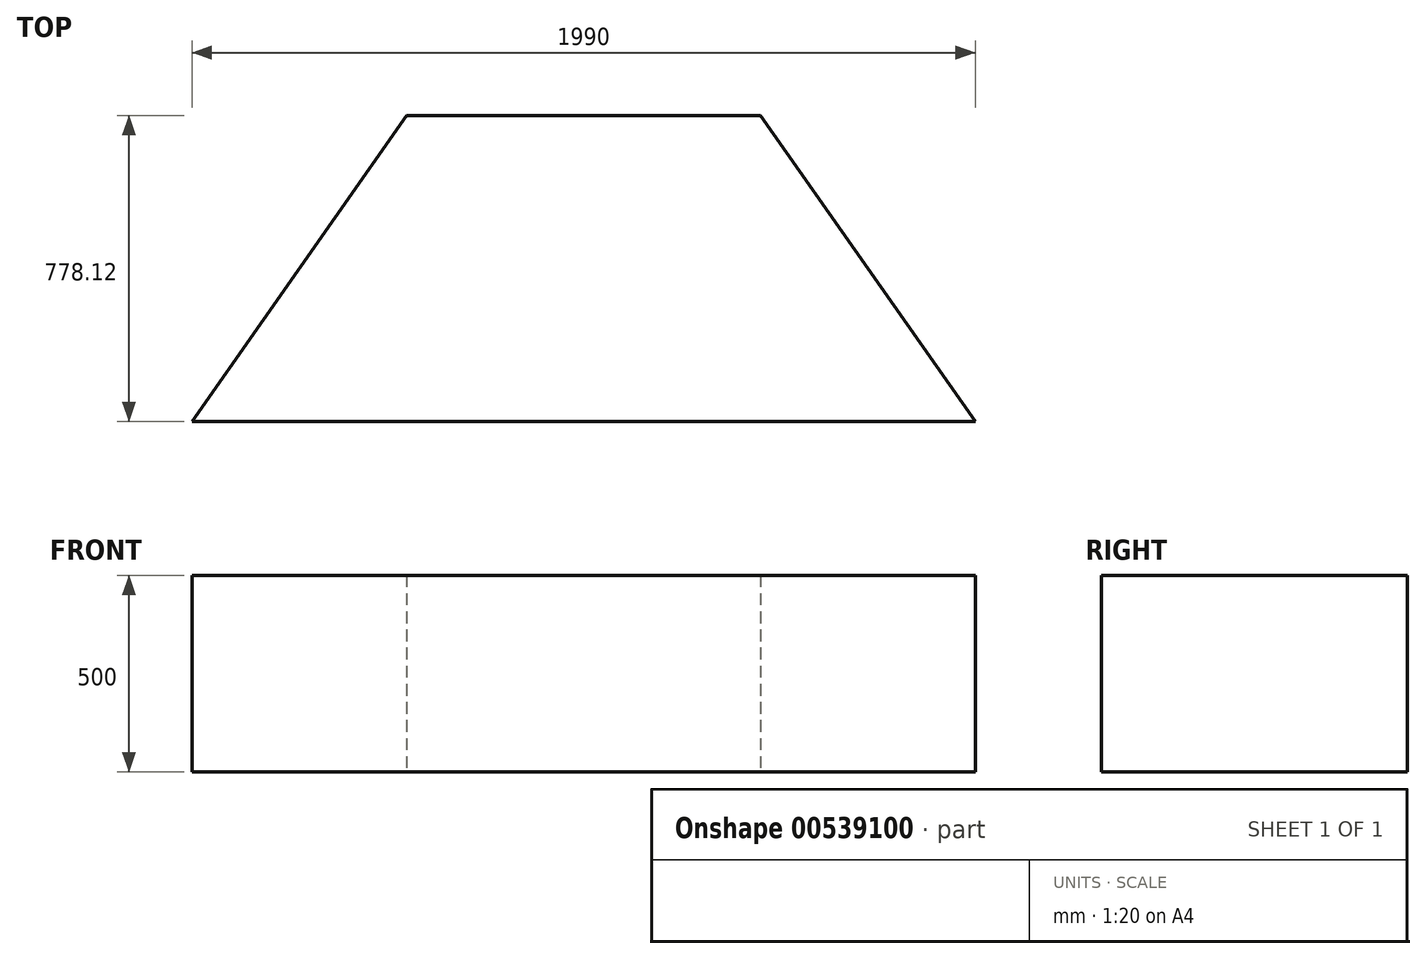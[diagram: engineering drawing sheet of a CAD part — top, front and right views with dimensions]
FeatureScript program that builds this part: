
annotation { "Feature Type Name" : "Feature", "Feature Type Description" : "" }
export const myFeature = defineFeature(function(context is Context, id is Id, definition is map)
    precondition{}
    {
        {
            var Q0;
            Q0=qCreatedBy(makeId("Top.planeOp"),FACE);
            var sketch = newSketch(context, id + "F0", { "sketchPlane" : qUnion([Q0])});
            skLineSegment(sketch, "E0", {"start": v(0, 0) * mm, "end": v(1990, 0) * mm});
            skLineSegment(sketch, "E1", {"start": v(0, 0) * mm, "end": v(545, 778.12) * mm});
            skLineSegment(sketch, "E2", {"start": v(1990, 0) * mm, "end": v(1445, 778.12) * mm});
            skLineSegment(sketch, "E3", {"start": v(545, 778.12) * mm, "end": v(1445, 778.12) * mm});
            skLineSegment(sketch, "E4", {"start": v(995, 778.12) * mm, "end": v(995, 0) * mm, "construction": true});
            skSolve(sketch);
        }
        {
            var Q0;
            Q0=makeQuery(id+"F0.imprint","IMPRINT",FACE,{"disambiguationData":[TD([[makeQuery(id+"F0.imprint","IMPRINT",EDGE,{"derivedFrom":sQuery(id+"F0.wireOp",EDGE,"E0")}),1.0]])]});
            extrude(context, id + "F1", {"entities" : qUnion([Q0]), "depth" : 500 * mm, "offsetDistance" : 25 * mm});
        }
    });
